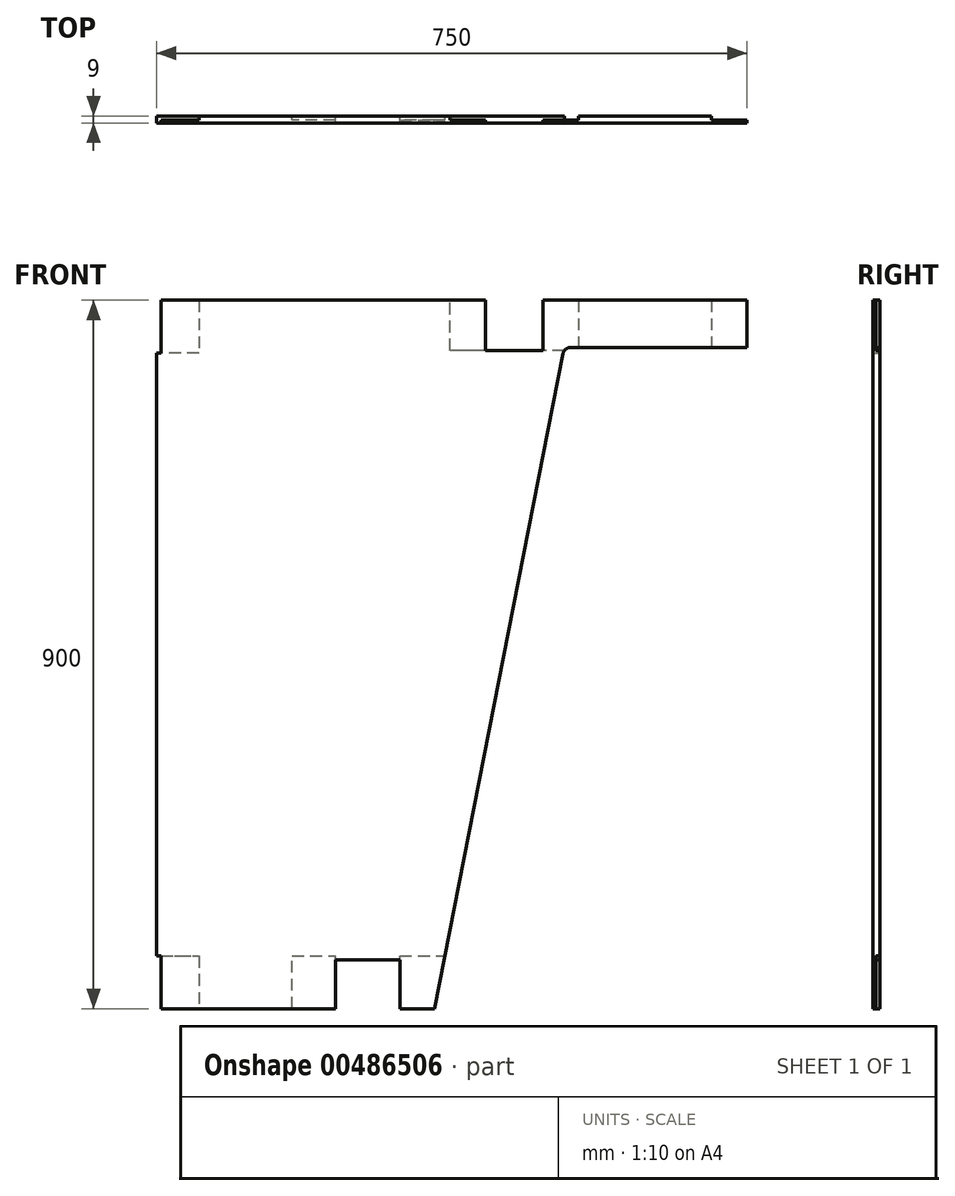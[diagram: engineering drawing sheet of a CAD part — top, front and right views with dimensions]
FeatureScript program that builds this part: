
annotation { "Feature Type Name" : "Feature", "Feature Type Description" : "" }
export const myFeature = defineFeature(function(context is Context, id is Id, definition is map)
    precondition{}
    {
        {
            var Q0;
            Q0=qCreatedBy(makeId("Front.planeOp"),FACE);
            var sketch = newSketch(context, id + "F0", { "sketchPlane" : qUnion([Q0])});
            skLineSegment(sketch, "E0", {"start": v(0, 900) * mm, "end": v(750, 900) * mm});
            skLineSegment(sketch, "E1", {"start": v(750, 900) * mm, "end": v(750, 840) * mm});
            skLineSegment(sketch, "E2", {"start": v(750, 840) * mm, "end": v(526.23, 840) * mm});
            skLineSegment(sketch, "E3", {"start": v(516.42, 831.92) * mm, "end": v(353.27, 0) * mm});
            skLineSegment(sketch, "E4", {"start": v(353.27, 0) * mm, "end": v(0, 0) * mm});
            skLineSegment(sketch, "E5", {"start": v(0, 900) * mm, "end": v(0, 0) * mm});
            skPoint(sketch, "E6.visualSharp", {"position": v(518, 840) * mm});
            skArc(sketch, "E6.filletArc", {"start": v(526.23, 840) * mm, "mid": v(519.88, 837.72) * mm, "end": v(516.42, 831.92) * mm});
            skLineSegment(sketch, "E7", {"start": v(54, 900) * mm, "end": v(54, 833) * mm});
            skLineSegment(sketch, "E8", {"start": v(54, 833) * mm, "end": v(0, 833) * mm});
            skLineSegment(sketch, "E9", {"start": v(705, 900) * mm, "end": v(705, 840) * mm});
            skLineSegment(sketch, "E10", {"start": v(491, 900) * mm, "end": v(491, 836) * mm});
            skLineSegment(sketch, "E11", {"start": v(491, 836) * mm, "end": v(418, 836) * mm});
            skLineSegment(sketch, "E12", {"start": v(418, 836) * mm, "end": v(418, 900) * mm});
            skLineSegment(sketch, "E13", {"start": v(418, 836) * mm, "end": v(373, 836) * mm});
            skLineSegment(sketch, "E14", {"start": v(373, 836) * mm, "end": v(373, 900) * mm});
            skLineSegment(sketch, "E15", {"start": v(491, 900) * mm, "end": v(536, 900) * mm});
            skLineSegment(sketch, "E16", {"start": v(536, 900) * mm, "end": v(536, 840) * mm});
            skLineSegment(sketch, "E17", {"start": v(518.23, 836) * mm, "end": v(491, 836) * mm});
            skLineSegment(sketch, "E18", {"start": v(309.27, 0) * mm, "end": v(309.27, 67) * mm});
            skLineSegment(sketch, "E19", {"start": v(309.27, 67) * mm, "end": v(366.4, 67) * mm});
            skLineSegment(sketch, "E20", {"start": v(227.27, 0) * mm, "end": v(227.27, 67) * mm});
            skLineSegment(sketch, "E21", {"start": v(227.27, 62) * mm, "end": v(309.27, 62) * mm});
            skLineSegment(sketch, "E22", {"start": v(172.27, 0) * mm, "end": v(172.27, 67) * mm});
            skLineSegment(sketch, "E23", {"start": v(172.27, 67) * mm, "end": v(227.27, 67) * mm});
            skLineSegment(sketch, "E24", {"start": v(6, 900) * mm, "end": v(6, 833) * mm});
            skLineSegment(sketch, "E25", {"start": v(0, 67) * mm, "end": v(54, 67) * mm});
            skLineSegment(sketch, "E26", {"start": v(54, 67) * mm, "end": v(54, 0) * mm});
            skLineSegment(sketch, "E27", {"start": v(6, 67) * mm, "end": v(6, 0) * mm});
            skSolve(sketch);
        }
        {
            var Q0;
            {var subQ3=sQuery(id+"F0.wireOp",EDGE,"E7");Q0=makeQuery(id+"F0.imprint","IMPRINT",FACE,{"disambiguationData":[TD([[makeQuery(id+"F0.imprint","IMPRINT",EDGE,{"derivedFrom":subQ3}),-1.0]])]});}
            var Q1;
            {var subQ0=sQuery(id+"F0.wireOp",EDGE,"E1");Q1=makeQuery(id+"F0.imprint","IMPRINT",FACE,{"disambiguationData":[TD([[makeQuery(id+"F0.imprint","IMPRINT",EDGE,{"derivedFrom":subQ0}),-1.0]])]});}
            var Q2;
            {var subQ0=sQuery(id+"F0.wireOp",EDGE,"E12");Q2=makeQuery(id+"F0.imprint","IMPRINT",FACE,{"disambiguationData":[TD([[makeQuery(id+"F0.imprint","IMPRINT",EDGE,{"derivedFrom":subQ0}),1.0]])]});}
            var Q3;
            {var subQ0=sQuery(id+"F0.wireOp",EDGE,"E9");Q3=makeQuery(id+"F0.imprint","IMPRINT",FACE,{"disambiguationData":[TD([[makeQuery(id+"F0.imprint","IMPRINT",EDGE,{"derivedFrom":subQ0}),-1.0]])]});}
            var Q4;
            {var subQ3=sQuery(id+"F0.wireOp",EDGE,"E3");Q4=makeQuery(id+"F0.imprint","IMPRINT",FACE,{"disambiguationData":[TD([[makeQuery(id+"F0.imprint","IMPRINT",EDGE,{"derivedFrom":subQ3}),-1.0]])]});}
            var Q5;
            Q5=makeQuery(id+"F0.imprint","IMPRINT",FACE,{"disambiguationData":[TD([[makeQuery(id+"F0.imprint","IMPRINT",EDGE,{"derivedFrom":sQuery(id+"F0.wireOp",EDGE,"E10")}),1.0]])]});
            var Q6;
            {var subQ1=sQuery(id+"F0.wireOp",EDGE,"E7");Q6=makeQuery(id+"F0.imprint","IMPRINT",FACE,{"disambiguationData":[TD([[makeQuery(id+"F0.imprint","IMPRINT",EDGE,{"derivedFrom":subQ1}),1.0]])]});}
            var Q7;
            {var subQ0=sQuery(id+"F0.wireOp",EDGE,"E22");Q7=makeQuery(id+"F0.imprint","IMPRINT",FACE,{"disambiguationData":[TD([[makeQuery(id+"F0.imprint","IMPRINT",EDGE,{"derivedFrom":subQ0}),-1.0]])]});}
            var Q8;
            {var subQ0=sQuery(id+"F0.wireOp",EDGE,"E26");Q8=makeQuery(id+"F0.imprint","IMPRINT",FACE,{"disambiguationData":[TD([[makeQuery(id+"F0.imprint","IMPRINT",EDGE,{"derivedFrom":subQ0}),-1.0]])]});}
            extrude(context, id + "F1", {"entities" : qUnion([Q0, Q1, Q2, Q3, Q4, Q5, Q6, Q7, Q8]), "depth" : 9 * mm, "offsetDistance" : 25 * mm});
        }
        {
            var Q0;
            {var subQ3=sQuery(id+"F0.wireOp",EDGE,"E7");Q0=makeQuery(id+"F0.imprint","IMPRINT",FACE,{"disambiguationData":[TD([[makeQuery(id+"F0.imprint","IMPRINT",EDGE,{"derivedFrom":subQ3}),-1.0]])]});}
            var Q1;
            {var subQ0=sQuery(id+"F0.wireOp",EDGE,"E1");Q1=makeQuery(id+"F0.imprint","IMPRINT",FACE,{"disambiguationData":[TD([[makeQuery(id+"F0.imprint","IMPRINT",EDGE,{"derivedFrom":subQ0}),-1.0]])]});}
            var Q2;
            {var subQ0=sQuery(id+"F0.wireOp",EDGE,"E12");Q2=makeQuery(id+"F0.imprint","IMPRINT",FACE,{"disambiguationData":[TD([[makeQuery(id+"F0.imprint","IMPRINT",EDGE,{"derivedFrom":subQ0}),1.0]])]});}
            var Q3;
            Q3=makeQuery(id+"F0.imprint","IMPRINT",FACE,{"disambiguationData":[TD([[makeQuery(id+"F0.imprint","IMPRINT",EDGE,{"derivedFrom":sQuery(id+"F0.wireOp",EDGE,"E10")}),1.0]])]});
            var Q4;
            {var subQ0=sQuery(id+"F0.wireOp",EDGE,"E19");Q4=makeQuery(id+"F0.imprint","IMPRINT",FACE,{"disambiguationData":[TD([[makeQuery(id+"F0.imprint","IMPRINT",EDGE,{"derivedFrom":subQ0}),-1.0]])]});}
            var Q5;
            {var subQ0=sQuery(id+"F0.wireOp",EDGE,"E22");Q5=makeQuery(id+"F0.imprint","IMPRINT",FACE,{"disambiguationData":[TD([[makeQuery(id+"F0.imprint","IMPRINT",EDGE,{"derivedFrom":subQ0}),-1.0]])]});}
            var Q6;
            {var subQ0=sQuery(id+"F0.wireOp",EDGE,"E26");Q6=makeQuery(id+"F0.imprint","IMPRINT",FACE,{"disambiguationData":[TD([[makeQuery(id+"F0.imprint","IMPRINT",EDGE,{"derivedFrom":subQ0}),-1.0]])]});}
            extrude(context, id + "F2", {"entities" : qUnion([Q0, Q1, Q2, Q3, Q4, Q5, Q6]), "operationType" : NewBodyOperationType.REMOVE, "depth" : 5 * mm, "offsetDistance" : 25 * mm});
        }
    });
